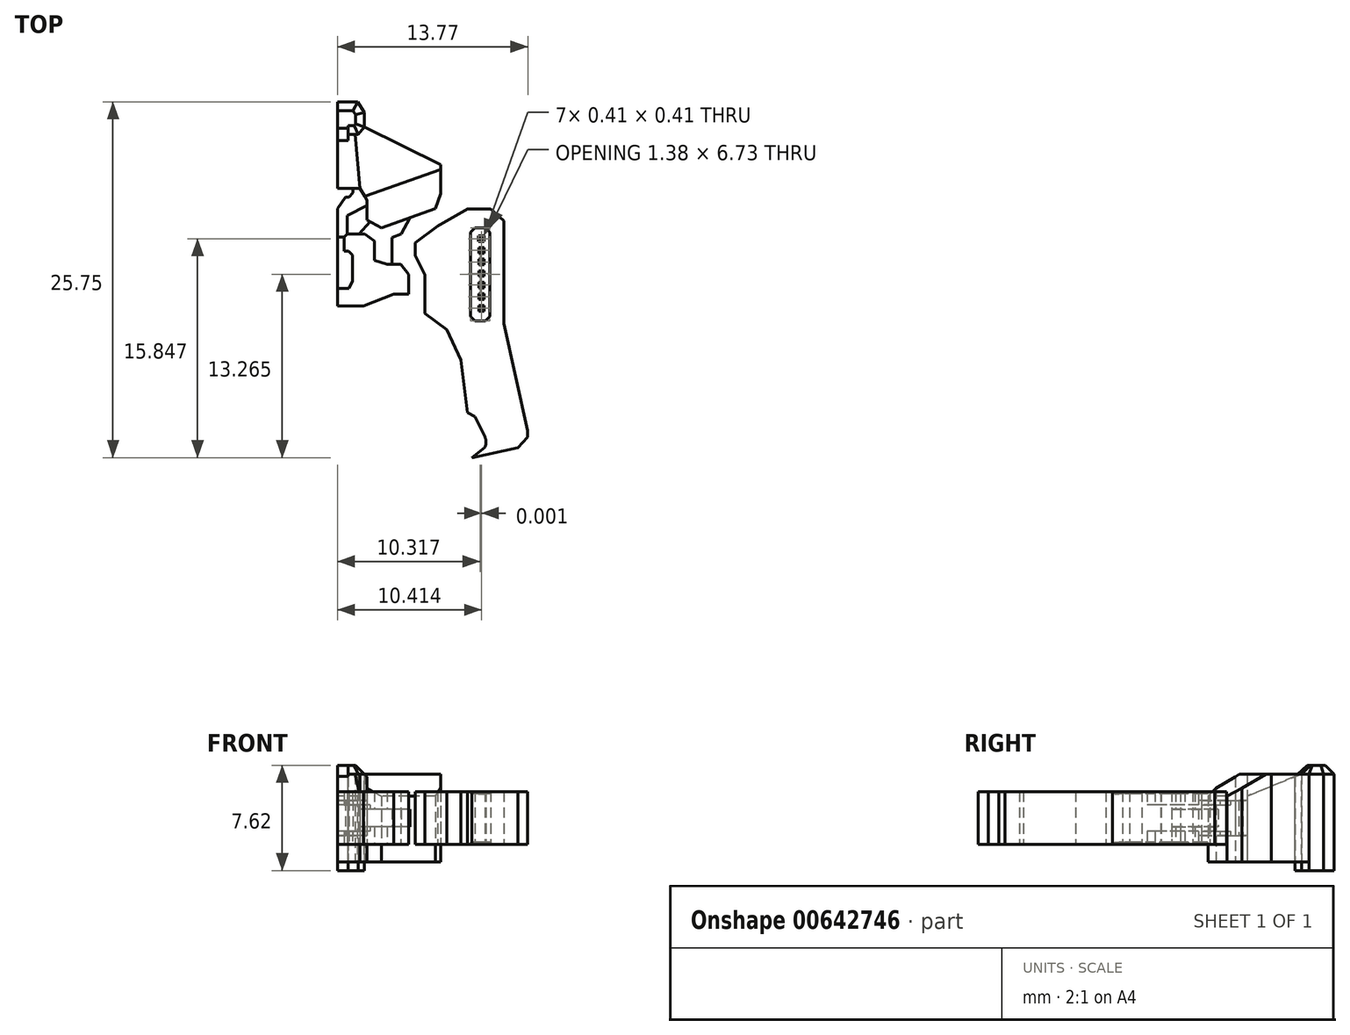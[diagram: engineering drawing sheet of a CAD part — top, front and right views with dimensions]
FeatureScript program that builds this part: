
annotation { "Feature Type Name" : "Feature", "Feature Type Description" : "" }
export const myFeature = defineFeature(function(context is Context, id is Id, definition is map)
    precondition{}
    {
        {
            var Q0;
            Q0=qCreatedBy(makeId("Top.planeOp"),FACE);
            var sketch = newSketch(context, id + "F0", { "sketchPlane" : qUnion([Q0])});
            skLineSegment(sketch, "E0", {"start": v(-50.93, 100.84) * mm, "end": v(-50.93, 0) * mm});
            skLineSegment(sketch, "E1", {"start": v(-43.79, 72.85) * mm, "end": v(-48.58, 77.57) * mm});
            skLineSegment(sketch, "E2", {"start": v(-50.93, 78.08) * mm, "end": v(-49.8, 78.08) * mm});
            skArc(sketch, "E3", {"start": v(-48.58, 77.57) * mm, "mid": v(-49.14, 77.94) * mm, "end": v(-49.8, 78.08) * mm});
            skLineSegment(sketch, "E4", {"start": v(-43.79, 72.85) * mm, "end": v(-43.46, 71.92) * mm});
            skLineSegment(sketch, "E5", {"start": v(-43.46, 71.92) * mm, "end": v(-48.98, 74.64) * mm});
            skLineSegment(sketch, "E6", {"start": v(-48.98, 74.64) * mm, "end": v(-48.98, 75.7) * mm});
            skLineSegment(sketch, "E7", {"start": v(-48.98, 75.7) * mm, "end": v(-49.45, 76.45) * mm});
            skLineSegment(sketch, "E8", {"start": v(-49.45, 76.45) * mm, "end": v(-50.93, 76.45) * mm});
            skLineSegment(sketch, "E9", {"start": v(-48.98, 74.64) * mm, "end": v(-49.43, 74.1) * mm});
            skLineSegment(sketch, "E10", {"start": v(-49.43, 74.1) * mm, "end": v(-50.17, 74.1) * mm});
            skLineSegment(sketch, "E11", {"start": v(-50.17, 74.1) * mm, "end": v(-50.17, 73.64) * mm});
            skLineSegment(sketch, "E12", {"start": v(-50.17, 73.64) * mm, "end": v(-50.93, 73.64) * mm});
            skLineSegment(sketch, "E13", {"start": v(-43.57, 72.22) * mm, "end": v(-42.36, 73.14) * mm});
            skLineSegment(sketch, "E14", {"start": v(-42.36, 73.14) * mm, "end": v(-40.44, 72.94) * mm});
            skLineSegment(sketch, "E15", {"start": v(-40.44, 72.94) * mm, "end": v(-37.18, 67.53) * mm});
            skLineSegment(sketch, "E16", {"start": v(-40.11, 72.4) * mm, "end": v(-42.04, 70.15) * mm});
            skLineSegment(sketch, "E17", {"start": v(-42.04, 70.15) * mm, "end": v(-42.6, 71.03) * mm});
            skLineSegment(sketch, "E18", {"start": v(-43.46, 71.92) * mm, "end": v(-43.46, 69.81) * mm});
            skLineSegment(sketch, "E19", {"start": v(-43.46, 69.81) * mm, "end": v(-43.83, 68.73) * mm});
            skLineSegment(sketch, "E20", {"start": v(-43.83, 68.73) * mm, "end": v(-47.76, 67.34) * mm});
            skLineSegment(sketch, "E21", {"start": v(-47.76, 67.34) * mm, "end": v(-48.79, 67.91) * mm});
            skLineSegment(sketch, "E22", {"start": v(-48.79, 67.91) * mm, "end": v(-48.79, 69.33) * mm});
            skLineSegment(sketch, "E23", {"start": v(-48.79, 69.33) * mm, "end": v(-49.3, 70.18) * mm});
            skLineSegment(sketch, "E24", {"start": v(-49.3, 70.18) * mm, "end": v(-50.93, 70.18) * mm});
            skLineSegment(sketch, "E25", {"start": v(-42.6, 71.03) * mm, "end": v(-43.46, 71.03) * mm});
            skLineSegment(sketch, "E26", {"start": v(-45.69, 68.08) * mm, "end": v(-46.34, 66.87) * mm});
            skLineSegment(sketch, "E27", {"start": v(-46.34, 66.87) * mm, "end": v(-46.98, 66.65) * mm});
            skLineSegment(sketch, "E28", {"start": v(-46.98, 66.65) * mm, "end": v(-46.98, 64.7) * mm});
            skLineSegment(sketch, "E29", {"start": v(-46.98, 64.7) * mm, "end": v(-47.35, 64.7) * mm});
            skLineSegment(sketch, "E30", {"start": v(-47.35, 64.7) * mm, "end": v(-48.26, 65) * mm});
            skLineSegment(sketch, "E31", {"start": v(-48.26, 65) * mm, "end": v(-48.26, 66.4) * mm});
            skLineSegment(sketch, "E32", {"start": v(-48.26, 66.4) * mm, "end": v(-48.95, 66.87) * mm});
            skLineSegment(sketch, "E33", {"start": v(-48.95, 66.87) * mm, "end": v(-50.23, 66.87) * mm});
            skLineSegment(sketch, "E34", {"start": v(-50.23, 66.87) * mm, "end": v(-50.46, 66.67) * mm});
            skLineSegment(sketch, "E35", {"start": v(-50.46, 66.67) * mm, "end": v(-50.46, 65.66) * mm});
            skLineSegment(sketch, "E36", {"start": v(-50.46, 65.66) * mm, "end": v(-50.13, 65.66) * mm});
            skLineSegment(sketch, "E37", {"start": v(-50.13, 65.66) * mm, "end": v(-49.85, 65.35) * mm});
            skLineSegment(sketch, "E38", {"start": v(-49.85, 65.35) * mm, "end": v(-49.85, 63.5) * mm});
            skLineSegment(sketch, "E39", {"start": v(-49.85, 63.5) * mm, "end": v(-50.1, 62.94) * mm});
            skLineSegment(sketch, "E40", {"start": v(-50.1, 62.94) * mm, "end": v(-50.93, 62.94) * mm});
            skLineSegment(sketch, "E41", {"start": v(-50.46, 66.67) * mm, "end": v(-50.93, 66.67) * mm});
            skLineSegment(sketch, "E42", {"start": v(-50.23, 66.87) * mm, "end": v(-50.23, 68.21) * mm});
            skLineSegment(sketch, "E43", {"start": v(-50.23, 68.21) * mm, "end": v(-48.79, 68.97) * mm});
            skLineSegment(sketch, "E44", {"start": v(-42.04, 70.15) * mm, "end": v(-41.88, 69.11) * mm});
            skLineSegment(sketch, "E45", {"start": v(-41.88, 69.11) * mm, "end": v(-43.68, 68.1) * mm});
            skLineSegment(sketch, "E46", {"start": v(-43.68, 68.1) * mm, "end": v(-43.68, 67.46) * mm});
            skLineSegment(sketch, "E47", {"start": v(-43.68, 67.46) * mm, "end": v(-45.3, 66.25) * mm});
            skLineSegment(sketch, "E48", {"start": v(-45.3, 66.25) * mm, "end": v(-45.3, 65.68) * mm});
            skLineSegment(sketch, "E49", {"start": v(-45.3, 65.68) * mm, "end": v(-45.99, 65.68) * mm});
            skLineSegment(sketch, "E50", {"start": v(-45.99, 65.68) * mm, "end": v(-46.36, 65.33) * mm});
            skLineSegment(sketch, "E51", {"start": v(-46.36, 65.33) * mm, "end": v(-46.36, 64.7) * mm});
            skLineSegment(sketch, "E52", {"start": v(-46.36, 64.7) * mm, "end": v(-46.98, 64.7) * mm});
            skLineSegment(sketch, "E53", {"start": v(-50.93, 61.68) * mm, "end": v(-49.04, 61.68) * mm});
            skLineSegment(sketch, "E54", {"start": v(-49.04, 61.68) * mm, "end": v(-46.85, 62.55) * mm});
            skLineSegment(sketch, "E55", {"start": v(-46.85, 62.55) * mm, "end": v(-45.77, 62.55) * mm});
            skLineSegment(sketch, "E56", {"start": v(-45.77, 62.55) * mm, "end": v(-45.77, 63.96) * mm});
            skLineSegment(sketch, "E57", {"start": v(-45.77, 63.96) * mm, "end": v(-46.36, 64.7) * mm});
            skLineSegment(sketch, "E58", {"start": v(-43.68, 67.46) * mm, "end": v(-41.52, 68.68) * mm});
            skLineSegment(sketch, "E59", {"start": v(-41.52, 68.68) * mm, "end": v(-39.85, 68.68) * mm});
            skLineSegment(sketch, "E60", {"start": v(-39.85, 68.68) * mm, "end": v(-38.88, 67.83) * mm});
            skLineSegment(sketch, "E61", {"start": v(-38.88, 67.83) * mm, "end": v(-38.88, 60.43) * mm});
            skLineSegment(sketch, "E62", {"start": v(-38.88, 60.43) * mm, "end": v(-37.16, 52.66) * mm});
            skLineSegment(sketch, "E63", {"start": v(-37.16, 52.66) * mm, "end": v(-37.16, 52.2) * mm});
            skLineSegment(sketch, "E64", {"start": v(-37.16, 52.2) * mm, "end": v(-37.9, 51.44) * mm});
            skLineSegment(sketch, "E65", {"start": v(-37.9, 51.44) * mm, "end": v(-41.88, 50.55) * mm});
            skLineSegment(sketch, "E66", {"start": v(-41.3, 67.01) * mm, "end": v(-41.3, 60.92) * mm});
            skLineSegment(sketch, "E67", {"start": v(-41.3, 60.92) * mm, "end": v(-40.98, 60.6) * mm});
            skLineSegment(sketch, "E68", {"start": v(-40.98, 60.6) * mm, "end": v(-40.24, 60.6) * mm});
            skLineSegment(sketch, "E69", {"start": v(-40.24, 60.6) * mm, "end": v(-39.92, 60.92) * mm});
            skLineSegment(sketch, "E70", {"start": v(-39.92, 60.92) * mm, "end": v(-39.92, 67.01) * mm});
            skLineSegment(sketch, "E71", {"start": v(-39.92, 67.01) * mm, "end": v(-40.24, 67.33) * mm});
            skLineSegment(sketch, "E72", {"start": v(-40.24, 67.33) * mm, "end": v(-40.98, 67.33) * mm});
            skLineSegment(sketch, "E73", {"start": v(-40.98, 67.33) * mm, "end": v(-41.3, 67.01) * mm});
            skLineSegment(sketch, "E74.bottom", {"start": v(-40.72, 66.75) * mm, "end": v(-40.31, 66.75) * mm});
            skLineSegment(sketch, "E74.top", {"start": v(-40.72, 66.34) * mm, "end": v(-40.31, 66.34) * mm});
            skLineSegment(sketch, "E74.left", {"start": v(-40.72, 66.75) * mm, "end": v(-40.72, 66.34) * mm});
            skLineSegment(sketch, "E74.right", {"start": v(-40.31, 66.75) * mm, "end": v(-40.31, 66.34) * mm});
            skLineSegment(sketch, "E75.1.0.0", {"start": v(-40.72, 65.91) * mm, "end": v(-40.31, 65.91) * mm});
            skLineSegment(sketch, "E75.1.0.1", {"start": v(-40.72, 65.91) * mm, "end": v(-40.72, 65.5) * mm});
            skLineSegment(sketch, "E75.1.0.2", {"start": v(-40.72, 65.5) * mm, "end": v(-40.31, 65.5) * mm});
            skLineSegment(sketch, "E75.1.0.3", {"start": v(-40.31, 65.91) * mm, "end": v(-40.31, 65.5) * mm});
            skLineSegment(sketch, "E75.2.0.0", {"start": v(-40.72, 65.07) * mm, "end": v(-40.31, 65.07) * mm});
            skLineSegment(sketch, "E75.2.0.1", {"start": v(-40.72, 65.07) * mm, "end": v(-40.72, 64.67) * mm});
            skLineSegment(sketch, "E75.2.0.2", {"start": v(-40.72, 64.67) * mm, "end": v(-40.31, 64.67) * mm});
            skLineSegment(sketch, "E75.2.0.3", {"start": v(-40.31, 65.07) * mm, "end": v(-40.31, 64.67) * mm});
            skLineSegment(sketch, "E75.3.0.0", {"start": v(-40.72, 64.24) * mm, "end": v(-40.3, 64.24) * mm});
            skLineSegment(sketch, "E75.3.0.1", {"start": v(-40.72, 64.24) * mm, "end": v(-40.72, 63.83) * mm});
            skLineSegment(sketch, "E75.3.0.2", {"start": v(-40.72, 63.83) * mm, "end": v(-40.3, 63.83) * mm});
            skLineSegment(sketch, "E75.3.0.3", {"start": v(-40.3, 64.24) * mm, "end": v(-40.3, 63.83) * mm});
            skLineSegment(sketch, "E75.4.0.0", {"start": v(-40.71, 63.4) * mm, "end": v(-40.3, 63.4) * mm});
            skLineSegment(sketch, "E75.4.0.1", {"start": v(-40.71, 63.4) * mm, "end": v(-40.71, 63) * mm});
            skLineSegment(sketch, "E75.4.0.2", {"start": v(-40.71, 63) * mm, "end": v(-40.3, 63) * mm});
            skLineSegment(sketch, "E75.4.0.3", {"start": v(-40.3, 63.4) * mm, "end": v(-40.3, 63) * mm});
            skLineSegment(sketch, "E75.5.0.0", {"start": v(-40.71, 62.56) * mm, "end": v(-40.3, 62.56) * mm});
            skLineSegment(sketch, "E75.5.0.1", {"start": v(-40.71, 62.56) * mm, "end": v(-40.71, 62.15) * mm});
            skLineSegment(sketch, "E75.5.0.2", {"start": v(-40.71, 62.15) * mm, "end": v(-40.3, 62.15) * mm});
            skLineSegment(sketch, "E75.5.0.3", {"start": v(-40.3, 62.56) * mm, "end": v(-40.3, 62.15) * mm});
            skLineSegment(sketch, "E75.6.0.0", {"start": v(-40.71, 61.72) * mm, "end": v(-40.3, 61.72) * mm});
            skLineSegment(sketch, "E75.6.0.1", {"start": v(-40.71, 61.72) * mm, "end": v(-40.71, 61.31) * mm});
            skLineSegment(sketch, "E75.6.0.2", {"start": v(-40.71, 61.31) * mm, "end": v(-40.3, 61.31) * mm});
            skLineSegment(sketch, "E75.6.0.3", {"start": v(-40.3, 61.72) * mm, "end": v(-40.3, 61.31) * mm});
            skLineSegment(sketch, "E75.direction1", {"start": v(-40.72, 66.75) * mm, "end": v(-40.72, 65.91) * mm, "construction": true});
            skLineSegment(sketch, "E76", {"start": v(-45.3, 65.68) * mm, "end": v(-45.3, 65.34) * mm});
            skLineSegment(sketch, "E77", {"start": v(-45.3, 65.34) * mm, "end": v(-44.6, 63.92) * mm});
            skLineSegment(sketch, "E78", {"start": v(-44.6, 63.92) * mm, "end": v(-44.6, 61.15) * mm});
            skLineSegment(sketch, "E79", {"start": v(-44.6, 61.15) * mm, "end": v(-43.03, 59.96) * mm});
            skLineSegment(sketch, "E80", {"start": v(-43.03, 59.96) * mm, "end": v(-42, 57.76) * mm});
            skLineSegment(sketch, "E81", {"start": v(-42, 57.76) * mm, "end": v(-41.53, 53.98) * mm});
            skLineSegment(sketch, "E82", {"start": v(-41.53, 53.98) * mm, "end": v(-40.98, 53.7) * mm});
            skLineSegment(sketch, "E83", {"start": v(-40.98, 53.7) * mm, "end": v(-40.27, 52.21) * mm});
            skArc(sketch, "E84", {"start": v(-40.27, 51.44) * mm, "mid": v(-40.18, 51.83) * mm, "end": v(-40.27, 52.21) * mm});
            skLineSegment(sketch, "E85", {"start": v(-40.27, 51.44) * mm, "end": v(-41.2, 50.7) * mm});
            skLineSegment(sketch, "E86", {"start": v(-49.98, 61.68) * mm, "end": v(-49.98, 60.83) * mm});
            skLineSegment(sketch, "E87", {"start": v(-49.98, 60.83) * mm, "end": v(-50.18, 60.66) * mm});
            skLineSegment(sketch, "E88", {"start": v(-50.18, 60.66) * mm, "end": v(-50.18, 60.13) * mm});
            skLineSegment(sketch, "E89", {"start": v(-50.18, 60.13) * mm, "end": v(-49.85, 59.72) * mm});
            skLineSegment(sketch, "E90", {"start": v(-49.85, 59.72) * mm, "end": v(-49.55, 59.72) * mm});
            skLineSegment(sketch, "E91", {"start": v(-49.55, 59.72) * mm, "end": v(-49.55, 56.77) * mm});
            skLineSegment(sketch, "E92", {"start": v(-49.55, 56.77) * mm, "end": v(-49.04, 56.39) * mm});
            skLineSegment(sketch, "E93", {"start": v(-49.04, 56.39) * mm, "end": v(-48.3, 56.39) * mm});
            skLineSegment(sketch, "E94", {"start": v(-48.3, 56.39) * mm, "end": v(-47.94, 55.98) * mm});
            skLineSegment(sketch, "E95", {"start": v(-47.94, 55.98) * mm, "end": v(-47.94, 52.69) * mm});
            skLineSegment(sketch, "E96", {"start": v(-47.94, 52.69) * mm, "end": v(-47.68, 52.45) * mm});
            skLineSegment(sketch, "E97", {"start": v(-47.68, 52.45) * mm, "end": v(-46.43, 52.45) * mm});
            skLineSegment(sketch, "E98", {"start": v(-46.43, 52.45) * mm, "end": v(-46.15, 52.67) * mm});
            skLineSegment(sketch, "E99", {"start": v(-46.15, 52.67) * mm, "end": v(-46.15, 55.45) * mm});
            skLineSegment(sketch, "E100", {"start": v(-46.15, 55.45) * mm, "end": v(-46.71, 57.53) * mm});
            skLineSegment(sketch, "E101", {"start": v(-46.71, 57.53) * mm, "end": v(-47.67, 59.56) * mm});
            skLineSegment(sketch, "E102", {"start": v(-47.67, 59.56) * mm, "end": v(-47.9, 59.56) * mm});
            skLineSegment(sketch, "E103", {"start": v(-47.9, 59.56) * mm, "end": v(-48.7, 60.39) * mm});
            skLineSegment(sketch, "E104", {"start": v(-48.7, 60.39) * mm, "end": v(-49.08, 60.39) * mm});
            skLineSegment(sketch, "E105", {"start": v(-49.08, 60.39) * mm, "end": v(-49.55, 59.72) * mm});
            skLineSegment(sketch, "E106", {"start": v(-48.7, 60.39) * mm, "end": v(-46.2, 60.97) * mm});
            skLineSegment(sketch, "E107", {"start": v(-46.2, 60.97) * mm, "end": v(-44.6, 61.15) * mm});
            skLineSegment(sketch, "E108", {"start": v(-46.15, 52.67) * mm, "end": v(-42.01, 53.2) * mm});
            skLineSegment(sketch, "E109", {"start": v(-42.01, 53.2) * mm, "end": v(-41.53, 53.98) * mm});
            skLineSegment(sketch, "E110", {"start": v(-48.57, 67.79) * mm, "end": v(-49.38, 66.87) * mm});
            skLineSegment(sketch, "E111", {"start": v(-50.63, 70.18) * mm, "end": v(-50.63, 71.22) * mm});
            skLineSegment(sketch, "E112", {"start": v(-50.63, 71.22) * mm, "end": v(-50.15, 71.22) * mm});
            skLineSegment(sketch, "E113", {"start": v(-50.15, 71.22) * mm, "end": v(-49.82, 70.88) * mm});
            skLineSegment(sketch, "E114", {"start": v(-49.82, 70.88) * mm, "end": v(-49.82, 70.18) * mm});
            skLineSegment(sketch, "E115", {"start": v(-49.82, 70.18) * mm, "end": v(-49.82, 69.87) * mm});
            skLineSegment(sketch, "E116", {"start": v(-49.82, 69.87) * mm, "end": v(-50.1, 69.56) * mm});
            skLineSegment(sketch, "E117", {"start": v(-50.1, 69.56) * mm, "end": v(-50.63, 69.56) * mm});
            skLineSegment(sketch, "E118", {"start": v(-50.63, 69.56) * mm, "end": v(-50.63, 70.18) * mm});
            skLineSegment(sketch, "E119", {"start": v(-50.93, 68.72) * mm, "end": v(-50.37, 69.56) * mm});
            skLineSegment(sketch, "E120", {"start": v(-49.3, 70.18) * mm, "end": v(-49.67, 74.1) * mm});
            skLineSegment(sketch, "E121", {"start": v(-42.36, 73.14) * mm, "end": v(-42.8, 73.63) * mm});
            skLineSegment(sketch, "E122", {"start": v(-42.8, 73.63) * mm, "end": v(-40.93, 77.35) * mm});
            skLineSegment(sketch, "E123", {"start": v(-40.93, 77.35) * mm, "end": v(-38.39, 77.61) * mm});
            skLineSegment(sketch, "E124", {"start": v(-38.39, 77.61) * mm, "end": v(-32.52, 74.18) * mm});
            skLineSegment(sketch, "E125", {"start": v(-32.52, 74.18) * mm, "end": v(-32.52, 68.13) * mm});
            skLineSegment(sketch, "E126", {"start": v(-32.52, 68.13) * mm, "end": v(-34.85, 66.73) * mm});
            skLineSegment(sketch, "E127", {"start": v(-34.85, 66.73) * mm, "end": v(-37.18, 67.53) * mm});
            skLineSegment(sketch, "E128", {"start": v(-34.3, 67.06) * mm, "end": v(-34.19, 66.31) * mm});
            skLineSegment(sketch, "E129", {"start": v(-34.19, 66.31) * mm, "end": v(-31.44, 65.36) * mm});
            skLineSegment(sketch, "E130", {"start": v(-31.44, 65.36) * mm, "end": v(-31.44, 63.66) * mm});
            skLineSegment(sketch, "E131", {"start": v(-31.44, 63.66) * mm, "end": v(-25.27, 58.77) * mm});
            skLineSegment(sketch, "E132", {"start": v(-25.27, 58.77) * mm, "end": v(-21.7, 56.27) * mm});
            skLineSegment(sketch, "E133", {"start": v(-21.7, 56.27) * mm, "end": v(-15.81, 44.84) * mm});
            skLineSegment(sketch, "E134", {"start": v(-15.81, 44.84) * mm, "end": v(-14.98, 44.84) * mm});
            skLineSegment(sketch, "E135", {"start": v(-14.98, 44.84) * mm, "end": v(-14.08, 44.22) * mm});
            skLineSegment(sketch, "E136", {"start": v(-14.08, 44.22) * mm, "end": v(-16.63, 43.55) * mm});
            skLineSegment(sketch, "E137", {"start": v(-16.63, 43.55) * mm, "end": v(-24.34, 58.12) * mm});
            skLineSegment(sketch, "E138", {"start": v(-41.96, 69.63) * mm, "end": v(-41.23, 69.63) * mm});
            skLineSegment(sketch, "E139", {"start": v(-41.23, 69.63) * mm, "end": v(-39.34, 71.12) * mm});
            skLineSegment(sketch, "E140", {"start": v(-39.7, 68.55) * mm, "end": v(-38.5, 69.73) * mm});
            skLineSegment(sketch, "E141", {"start": v(-37.18, 67.53) * mm, "end": v(-38.16, 63.8) * mm});
            skLineSegment(sketch, "E142", {"start": v(-38.16, 63.8) * mm, "end": v(-36.91, 63.36) * mm});
            skLineSegment(sketch, "E143", {"start": v(-36.91, 63.36) * mm, "end": v(-36.13, 63.5) * mm});
            skLineSegment(sketch, "E144", {"start": v(-35.41, 66.92) * mm, "end": v(-36.45, 62) * mm});
            skLineSegment(sketch, "E145", {"start": v(-36.45, 62) * mm, "end": v(-33.82, 61.64) * mm});
            skLineSegment(sketch, "E146", {"start": v(-50.93, 55.98) * mm, "end": v(-49.04, 55.98) * mm});
            skLineSegment(sketch, "E147", {"start": v(-49.04, 55.98) * mm, "end": v(-48.54, 55.5) * mm});
            skLineSegment(sketch, "E148", {"start": v(-48.54, 55.5) * mm, "end": v(-48.54, 52.69) * mm});
            skLineSegment(sketch, "E149", {"start": v(-48.54, 52.69) * mm, "end": v(-47.95, 51.02) * mm});
            skLineSegment(sketch, "E150", {"start": v(-47.95, 51.02) * mm, "end": v(-48.19, 50.55) * mm});
            skLineSegment(sketch, "E151", {"start": v(-48.19, 50.55) * mm, "end": v(-49.82, 49.75) * mm});
            skLineSegment(sketch, "E152", {"start": v(-49.82, 49.75) * mm, "end": v(-50.7, 52.2) * mm});
            skLineSegment(sketch, "E153", {"start": v(-50.7, 52.2) * mm, "end": v(-50.93, 52.2) * mm});
            skLineSegment(sketch, "E154", {"start": v(-50.93, 50.07) * mm, "end": v(-50.67, 50.07) * mm});
            skLineSegment(sketch, "E155", {"start": v(-50.67, 50.07) * mm, "end": v(-50.37, 49.75) * mm});
            skLineSegment(sketch, "E156", {"start": v(-50.37, 49.75) * mm, "end": v(-49.82, 49.75) * mm});
            skLineSegment(sketch, "E157", {"start": v(-48.54, 55.22) * mm, "end": v(-47.94, 55.22) * mm});
            skLineSegment(sketch, "E158", {"start": v(-48.54, 53.77) * mm, "end": v(-47.94, 53.77) * mm});
            skSolve(sketch);
        }
        {
            var Q0;
            {var subQ0=sQuery(id+"F0.wireOp",EDGE,"E111");Q0=makeQuery(id+"F0.imprint","IMPRINT",FACE,{"disambiguationData":[TD([[makeQuery(id+"F0.imprint","IMPRINT",EDGE,{"derivedFrom":subQ0}),-1.0]])]});}
            var Q1;
            {var subQ6=sQuery(id+"F0.wireOp",EDGE,"E11");Q1=makeQuery(id+"F0.imprint","IMPRINT",FACE,{"disambiguationData":[TD([[makeQuery(id+"F0.imprint","IMPRINT",EDGE,{"derivedFrom":subQ6}),1.0]])]});}
            extrude(context, id + "F1", {"entities" : qUnion([Q0, Q1]), "endBound" : BoundingType.SYMMETRIC, "depth" : 6.35 * mm, "offsetDistance" : 25.4 * mm});
        }
        {
            var Q0;
            {var subQ6=sQuery(id+"F0.wireOp",EDGE,"E26");Q0=makeQuery(id+"F0.imprint","IMPRINT",FACE,{"disambiguationData":[TD([[makeQuery(id+"F0.imprint","IMPRINT",EDGE,{"derivedFrom":subQ6}),-1.0]])]});}
            extrude(context, id + "F2", {"entities" : qUnion([Q0]), "operationType" : NewBodyOperationType.ADD, "endBound" : BoundingType.SYMMETRIC, "depth" : 1.27 * mm, "offsetDistance" : 25.4 * mm});
        }
        {
            var Q0;
            {var subQ0=sQuery(id+"F0.wireOp",EDGE,"E42");Q0=makeQuery(id+"F0.imprint","IMPRINT",FACE,{"disambiguationData":[TD([[makeQuery(id+"F0.imprint","IMPRINT",EDGE,{"derivedFrom":subQ0}),-1.0]])]});}
            extrude(context, id + "F3", {"entities" : qUnion([Q0]), "operationType" : NewBodyOperationType.ADD, "endBound" : BoundingType.SYMMETRIC, "depth" : 1.9 * mm, "offsetDistance" : 25.4 * mm});
        }
        {
            var Q0;
            {var subQ1=sQuery(id+"F0.wireOp",EDGE,"E23");Q0=makeQuery(id+"F0.imprint","IMPRINT",FACE,{"disambiguationData":[TD([[makeQuery(id+"F0.imprint","IMPRINT",EDGE,{"derivedFrom":subQ1}),1.0]])]});}
            extrude(context, id + "F4", {"entities" : qUnion([Q0]), "operationType" : NewBodyOperationType.ADD, "endBound" : BoundingType.SYMMETRIC, "depth" : 2.54 * mm, "offsetDistance" : 25.4 * mm});
        }
        {
            var Q0;
            Q0=makeQuery(id+"F0.imprint","IMPRINT",FACE,{"disambiguationData":[TD([[makeQuery(id+"F0.imprint","IMPRINT",EDGE,{"derivedFrom":sQuery(id+"F0.wireOp",EDGE,"E35")}),-1.0]])]});
            extrude(context, id + "F5", {"entities" : qUnion([Q0]), "operationType" : NewBodyOperationType.ADD, "endBound" : BoundingType.SYMMETRIC, "depth" : 1.9 * mm, "offsetDistance" : 25.4 * mm});
        }
        {
            var Q0;
            Q0=makeQuery(id+"F0.imprint","IMPRINT",FACE,{"disambiguationData":[TD([[makeQuery(id+"F0.imprint","IMPRINT",EDGE,{"derivedFrom":sQuery(id+"F0.wireOp",EDGE,"E29")}),1.0]])]});
            extrude(context, id + "F6", {"entities" : qUnion([Q0]), "operationType" : NewBodyOperationType.ADD, "endBound" : BoundingType.SYMMETRIC, "depth" : 3.8 * mm, "offsetDistance" : 25.4 * mm});
        }
        {
            var Q0;
            Q0=makeQuery(id+"F0.imprint","IMPRINT",FACE,{"disambiguationData":[TD([[makeQuery(id+"F0.imprint","IMPRINT",EDGE,{"derivedFrom":sQuery(id+"F0.wireOp",EDGE,"E47")}),1.0]])]});
            extrude(context, id + "F7", {"entities" : qUnion([Q0]), "endBound" : BoundingType.SYMMETRIC, "depth" : 3.8 * mm, "offsetDistance" : 25.4 * mm});
        }
        {
            var Q0;
            Q0=makeQuery(id+"F1.opExtrude","CAP_EDGE",EDGE,{"disambiguationData":[OSD([sQuery(id+"F0.wireOp",EDGE,"E24")])],"isStart":false});
            chamfer(context, id + "F8", {"entities" : qUnion([Q0]), "chamferType" : ChamferType.TWO_OFFSETS, "width1" : 1.59 * mm, "oppositeDirection" : false, "width2" : 3.92 * mm, "tangentPropagation" : true});
        }
        {
            var Q0;
            {var subQ8=sQuery(id+"F0.wireOp",EDGE,"E5");Q0=makeQuery(id+"F0.imprint","IMPRINT",FACE,{"disambiguationData":[TD([[makeQuery(id+"F0.imprint","IMPRINT",EDGE,{"derivedFrom":subQ8}),1.0]])]});}
            extrude(context, id + "F9", {"entities" : qUnion([Q0]), "endBound" : BoundingType.SYMMETRIC, "depth" : 6.35 * mm, "offsetDistance" : 25.4 * mm});
        }
        {
            var Q0;
            Q0=makeQuery(id+"F9.opExtrude","CAP_EDGE",EDGE,{"disambiguationData":[OSD([sQuery(id+"F0.wireOp",EDGE,"E20")])],"isStart":false});
            chamfer(context, id + "F10", {"entities" : qUnion([Q0]), "chamferType" : ChamferType.TWO_OFFSETS, "width1" : 1.59 * mm, "oppositeDirection" : false, "width2" : 2.54 * mm, "tangentPropagation" : true});
        }
        {
            var Q0;
            Q0=makeQuery(id+"F0.imprint","IMPRINT",FACE,{"disambiguationData":[TD([[makeQuery(id+"F0.imprint","IMPRINT",EDGE,{"derivedFrom":sQuery(id+"F0.wireOp",EDGE,"E66")}),1.0]])]});
            extrude(context, id + "F11", {"entities" : qUnion([Q0]), "operationType" : NewBodyOperationType.ADD, "endBound" : BoundingType.SYMMETRIC, "depth" : 3.5 * mm, "offsetDistance" : 25.4 * mm});
        }
        {
            var Q0;
            Q0=makeQuery(id+"F0.imprint","IMPRINT",FACE,{"disambiguationData":[TD([[makeQuery(id+"F0.imprint","IMPRINT",EDGE,{"derivedFrom":sQuery(id+"F0.wireOp",EDGE,"E74.bottom")}),-1.0]])]});
            var Q1;
            Q1=makeQuery(id+"F0.imprint","IMPRINT",FACE,{"disambiguationData":[TD([[makeQuery(id+"F0.imprint","IMPRINT",EDGE,{"derivedFrom":sQuery(id+"F0.wireOp",EDGE,"E75.1.0.0")}),-1.0]])]});
            var Q2;
            Q2=makeQuery(id+"F0.imprint","IMPRINT",FACE,{"disambiguationData":[TD([[makeQuery(id+"F0.imprint","IMPRINT",EDGE,{"derivedFrom":sQuery(id+"F0.wireOp",EDGE,"E75.2.0.0")}),-1.0]])]});
            var Q3;
            Q3=makeQuery(id+"F0.imprint","IMPRINT",FACE,{"disambiguationData":[TD([[makeQuery(id+"F0.imprint","IMPRINT",EDGE,{"derivedFrom":sQuery(id+"F0.wireOp",EDGE,"E75.3.0.0")}),-1.0]])]});
            var Q4;
            Q4=makeQuery(id+"F0.imprint","IMPRINT",FACE,{"disambiguationData":[TD([[makeQuery(id+"F0.imprint","IMPRINT",EDGE,{"derivedFrom":sQuery(id+"F0.wireOp",EDGE,"E75.4.0.0")}),-1.0]])]});
            var Q5;
            Q5=makeQuery(id+"F0.imprint","IMPRINT",FACE,{"disambiguationData":[TD([[makeQuery(id+"F0.imprint","IMPRINT",EDGE,{"derivedFrom":sQuery(id+"F0.wireOp",EDGE,"E75.5.0.0")}),-1.0]])]});
            var Q6;
            Q6=makeQuery(id+"F0.imprint","IMPRINT",FACE,{"disambiguationData":[TD([[makeQuery(id+"F0.imprint","IMPRINT",EDGE,{"derivedFrom":sQuery(id+"F0.wireOp",EDGE,"E75.6.0.0")}),-1.0]])]});
            extrude(context, id + "F12", {"entities" : qUnion([Q0, Q1, Q2, Q3, Q4, Q5, Q6]), "operationType" : NewBodyOperationType.ADD, "endBound" : BoundingType.SYMMETRIC, "depth" : 3.62 * mm, "offsetDistance" : 25.4 * mm});
        }
        {
            var Q0;
            Q0=makeQuery(id+"F12.opExtrude","CAP_EDGE",EDGE,{"disambiguationData":[OSD([sQuery(id+"F0.wireOp",EDGE,"E75.6.0.3")])],"isStart":false});
            var Q1;
            Q1=makeQuery(id+"F12.opExtrude","CAP_EDGE",EDGE,{"disambiguationData":[OSD([sQuery(id+"F0.wireOp",EDGE,"E75.6.0.2")])],"isStart":false});
            var Q2;
            Q2=makeQuery(id+"F12.opExtrude","CAP_FACE",FACE,{"disambiguationData":[OSD([sQuery(id+"F0.wireOp",EDGE,"E74.bottom"),sQuery(id+"F0.wireOp",EDGE,"E74.top"),sQuery(id+"F0.wireOp",EDGE,"E74.left"),sQuery(id+"F0.wireOp",EDGE,"E74.right")])],"isStart":false});
            var Q3;
            Q3=makeQuery(id+"F12.opExtrude","CAP_FACE",FACE,{"disambiguationData":[OSD([sQuery(id+"F0.wireOp",EDGE,"E75.1.0.0"),sQuery(id+"F0.wireOp",EDGE,"E75.1.0.1"),sQuery(id+"F0.wireOp",EDGE,"E75.1.0.2"),sQuery(id+"F0.wireOp",EDGE,"E75.1.0.3")])],"isStart":false});
            var Q4;
            Q4=makeQuery(id+"F12.opExtrude","CAP_FACE",FACE,{"disambiguationData":[OSD([sQuery(id+"F0.wireOp",EDGE,"E75.2.0.0"),sQuery(id+"F0.wireOp",EDGE,"E75.2.0.1"),sQuery(id+"F0.wireOp",EDGE,"E75.2.0.2"),sQuery(id+"F0.wireOp",EDGE,"E75.2.0.3")])],"isStart":false});
            var Q5;
            Q5=makeQuery(id+"F12.opExtrude","CAP_FACE",FACE,{"disambiguationData":[OSD([sQuery(id+"F0.wireOp",EDGE,"E75.3.0.0"),sQuery(id+"F0.wireOp",EDGE,"E75.3.0.1"),sQuery(id+"F0.wireOp",EDGE,"E75.3.0.2"),sQuery(id+"F0.wireOp",EDGE,"E75.3.0.3")])],"isStart":false});
            var Q6;
            Q6=makeQuery(id+"F12.opExtrude","CAP_FACE",FACE,{"disambiguationData":[OSD([sQuery(id+"F0.wireOp",EDGE,"E75.4.0.0"),sQuery(id+"F0.wireOp",EDGE,"E75.4.0.1"),sQuery(id+"F0.wireOp",EDGE,"E75.4.0.2"),sQuery(id+"F0.wireOp",EDGE,"E75.4.0.3")])],"isStart":false});
            var Q7;
            Q7=makeQuery(id+"F12.opExtrude","CAP_FACE",FACE,{"disambiguationData":[OSD([sQuery(id+"F0.wireOp",EDGE,"E75.5.0.0"),sQuery(id+"F0.wireOp",EDGE,"E75.5.0.1"),sQuery(id+"F0.wireOp",EDGE,"E75.5.0.2"),sQuery(id+"F0.wireOp",EDGE,"E75.5.0.3")])],"isStart":false});
            var Q8;
            Q8=makeQuery(id+"F12.opExtrude","CAP_FACE",FACE,{"disambiguationData":[OSD([sQuery(id+"F0.wireOp",EDGE,"E75.6.0.0"),sQuery(id+"F0.wireOp",EDGE,"E75.6.0.1"),sQuery(id+"F0.wireOp",EDGE,"E75.6.0.2"),sQuery(id+"F0.wireOp",EDGE,"E75.6.0.3")])],"isStart":false});
            chamfer(context, id + "F13", {"entities" : qUnion([Q0, Q1, Q2, Q3, Q4, Q5, Q6, Q7, Q8]), "width" : 0.06 * mm, "tangentPropagation" : true});
        }
        {
            var Q0;
            Q0=makeQuery(id+"F0.imprint","IMPRINT",FACE,{"disambiguationData":[TD([[makeQuery(id+"F0.imprint","IMPRINT",EDGE,{"derivedFrom":sQuery(id+"F0.wireOp",EDGE,"E6")}),1.0]])]});
            extrude(context, id + "F14", {"entities" : qUnion([Q0]), "endBound" : BoundingType.SYMMETRIC, "oppositeDirection" : true, "depth" : 7.62 * mm, "offsetDistance" : 25.4 * mm});
        }
        {
            var Q0;
            Q0=makeQuery(id+"F14.opExtrude","CAP_EDGE",EDGE,{"disambiguationData":[OSD([sQuery(id+"F0.wireOp",EDGE,"E10")])],"isStart":true});
            var Q1;
            Q1=makeQuery(id+"F14.opExtrude","CAP_EDGE",EDGE,{"disambiguationData":[OSD([sQuery(id+"F0.wireOp",EDGE,"E9")])],"isStart":true});
            var Q2;
            Q2=makeQuery(id+"F14.opExtrude","CAP_EDGE",EDGE,{"disambiguationData":[OSD([sQuery(id+"F0.wireOp",EDGE,"E6")])],"isStart":true});
            var Q3;
            Q3=makeQuery(id+"F14.opExtrude","CAP_EDGE",EDGE,{"disambiguationData":[OSD([sQuery(id+"F0.wireOp",EDGE,"E7")])],"isStart":true});
            var Q4;
            Q4=makeQuery(id+"F14.opExtrude","CAP_EDGE",EDGE,{"disambiguationData":[OSD([sQuery(id+"F0.wireOp",EDGE,"E8")])],"isStart":true});
            chamfer(context, id + "F15", {"entities" : qUnion([Q0, Q1, Q2, Q3, Q4]), "width" : 0.64 * mm, "tangentPropagation" : true});
        }
        {
            var Q0;
            Q0=makeQuery(id+"F14.opExtrude","CAP_EDGE",EDGE,{"disambiguationData":[OSD([sQuery(id+"F0.wireOp",EDGE,"E12")])],"isStart":true});
            chamfer(context, id + "F16", {"entities" : qUnion([Q0]), "chamferType" : ChamferType.TWO_OFFSETS, "width1" : 0.82 * mm, "oppositeDirection" : false, "width2" : 0.89 * mm, "tangentPropagation" : true});
        }
    });
